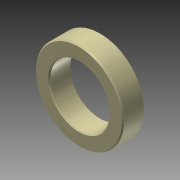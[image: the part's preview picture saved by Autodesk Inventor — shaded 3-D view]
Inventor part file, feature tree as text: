
AUTODESK INVENTOR PART (.ipt)
format: ipt  version: 2014 (Build 180170000, 170)  size: 111,616 bytes
history: native  units: in
note: dims shown in document units (in); Inventor stores cm internally (conversion verified against a paired STEP export)
features: extrude x1, chamfer x1, sketch x1
ambient origin geometry x8: Origin, YZ Plane, XZ Plane, XY Plane, X Axis, Y Axis, Z Axis, Center Point
bodies: Solid1 (feature_tree)
feature tree (3):
  extrude  "Extrusion1"  Depth=0.188in
  chamfer  "Chamfer1"  Distance=0.188in
  sketch  "Sketch1"  dims[d0=0.505in d1=0.75in d2=0.188in d3=0.0in d4=0.01in d5=0.125in d6=45.0deg]
